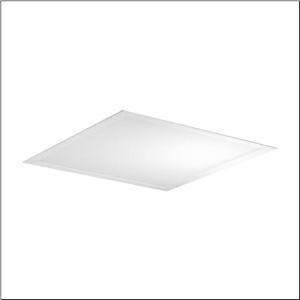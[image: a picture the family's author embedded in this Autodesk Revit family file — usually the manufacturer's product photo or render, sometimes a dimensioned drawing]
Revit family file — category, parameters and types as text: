
# Revit family: apollon_r__31_square_51mp11wd2n42_7747
name_source: partatom
category: Lighting Fixtures
units: mm (PartAtom-declared; Revit-internal decimal feet)

## family parameters
Cut with Voids When Loaded = No
Host = Face
Light Source = No
Part Type = Normal
Room Calculation Point = No
Round Connector Dimension = Use Diameter
Shared = No

## types (1)
- --- (1 x LED, 4000 lm, 27.5 W, 5000K)
    Apparent Load = 28 VA
    CIE Flux Codes = 62 87 97 100 100
    Color Rendering = 80
    Color Temperature = 5000K
    Default Elevation = 1800 mm
    Description = Apollon® 31 square, office luminaire, primary optical cover: micro prismatic cover, of PMMA, CAT 2 (L<= 3000cd/m²), light emission: direct distribution, primary light characteristic: symmetric, installation type: lay-in mounting, LED, rated luminous flux: 4.000lm, luminous efficacy: 145lm/W, light colour: 840/850, colour temperature: 4000/5000K, with terminal, 5-pole, mains connection: 220..240V, AC/DC, 0/50..60Hz, rated input power: 28W, housing, of aluminium, traffic white (RAL 9016), module: M625, length: 620mm, width: 620mm, height: 32mm, housing upper side, of sheet steel, galvanised, protection rating (complete): IP20, protection rating (on room side): IP40, insulation class (complete): insulation class II (safety insulation), certification: CE, ENEC, impact resistance: IK03, permissible operating ambient temperature: -20..+40°C, permissible storage temperature: -20..+60°C, packaging unit: 1 piece
    Height = 0 mm  [stored 0 ft]
    Lamp = 1 x LED
    Lamp Light Flux = 4000 lm
    Lamp Power = 27.5 W
    Lamp count = 1
    Length = 620 mm
    Luminous efficacy = 145 lm/W
    Manufacturer = Siteco
    ModVariant = No
    Model = 51MP11WD2N42
    Mounting Place = Ceiling
    Mounting Type = Recessed
    Number of Poles = 1
    OnlyDefault = Yes
    Power Factor = 1
    Product Name = Apollon® 31 square
    Product group = office luminaire | ceiling recessed
    ProductGroupID = 400
    Protection Class = Protection class II
    Protection Degree = IP 20
    RLX_Detail_Level = 1
    RLX_Emergency_Light_Flux = 0 lm
    RLX_Emergency_Type = 0
    RLX_Emergency_Type_DB = No
    RlxData = <blob elided: 13169 chars, md5=e1fd56d8>
    Socket = socket
    Standby Power = 0 W
    System Light Flux = 4000 lm
    System Power = 28 W
    Type Comments = individual setting: colour temperature 5000K
    Type Image = l_1291039.jpg
    URL = http://relux.com
    VarID = @adj_045647
    Voltage = 0 V
    Weight = 0.00 kg
    Width = 620 mm

note: [stored X ft] marks values corroborated as IEEE doubles in the binary element streams (Revit-internal decimal feet)

## geometry (parser evidence)
native form markers: Sweep x10
no freeform markers — native parametric forms only
